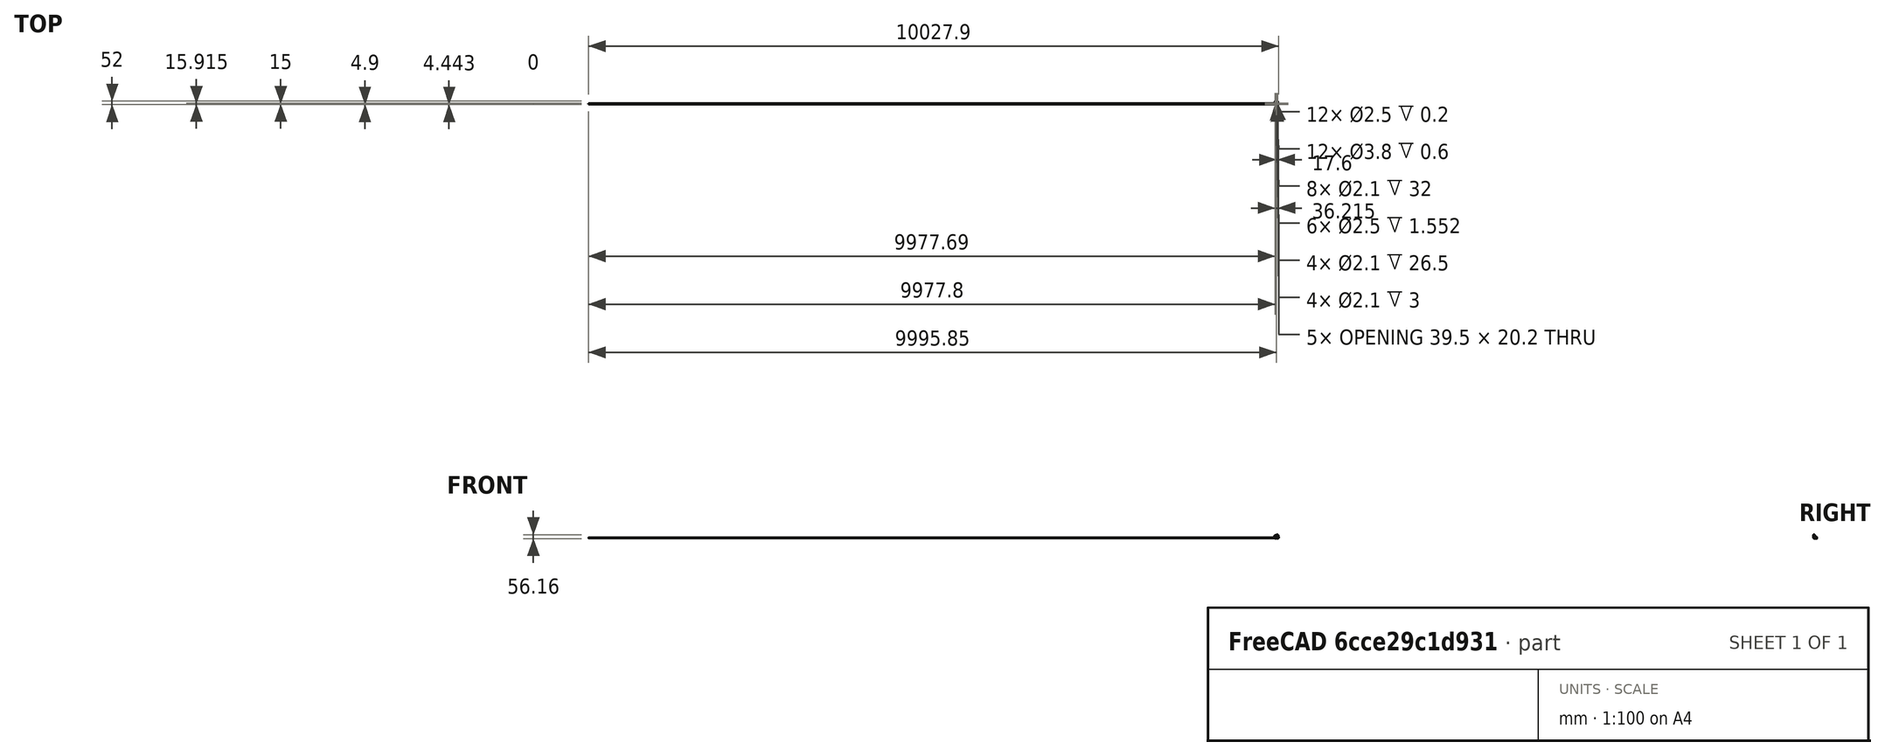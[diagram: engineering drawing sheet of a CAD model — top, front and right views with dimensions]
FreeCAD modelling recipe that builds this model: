
FCSTD DOCUMENT  (FreeCAD 0.14R3702 (Git))
Label: SM-S4303R
License: CC-BY 3.0
LicenseURL: http://creativecommons.org/licenses/by/3.0/
objects: Sketcher::SketchObject×27, Part::Feature×24, PartDesign::Pocket×12, PartDesign::Pad×9, Part::Fillet×7, Part::MultiFuse×6, App::DocumentObjectGroup×5, Part::Compound×4, Part::Loft×3, PartDesign::Mirrored×2, Part::Cut×2, PartDesign::Fillet×2, PartDesign::Chamfer×2, PartDesign::PolarPattern×1, Part::Cylinder×1
note: 123 computed .brp shape members not serialized (recipe doc carries the construction recipe); baked Part::Feature solids carry a one-line shape summary decoded from their .brp

FEATURE [Sketcher::SketchObject] Sketch  label="servo-body-sketch"
  Placement = pos=(0,0,0) rot=(1,0,0;1.5708rad)
  sketch-geometry (5):
    g0: LineSegment StartX=20.55 StartY=39.6 StartZ=0 EndX=20.55 EndY=0 EndZ=0
    g1: LineSegment StartX=20.55 StartY=0 StartZ=0 EndX=-20.55 EndY=0 EndZ=0
    g2: LineSegment StartX=-20.55 StartY=0 StartZ=0 EndX=-20.55 EndY=34.9 EndZ=0
    g3: LineSegment StartX=-20.55 StartY=34.9 StartZ=0 EndX=-12.25 EndY=39.6 EndZ=0
    g4: LineSegment StartX=-12.25 StartY=39.6 StartZ=0 EndX=20.55 EndY=39.6 EndZ=0
  constraints (15):
    c: Coincident(g0,g1)
    c: Coincident(g1,g2)
    c: Horizontal(g1)
    c: Vertical(g0)
    c: Vertical(g2)
    c: Symmetric(g1,g0,g-2)
    c: PointOnObject(g1,g-1)
    c: DistanceX(g1) = -41.1
    c: DistanceY(g0) = -39.6
    c: Coincident(g3,g2)
    c: Horizontal(g4)
    c: Coincident(g4,g0)
    c: Coincident(g3,g4)
    c: DistanceY(g2) = 34.9
    c: DistanceX(g4) = 32.8
FEATURE [PartDesign::Pad] Pad  label="servo-body-1"
  Length = 20.8
  Length2 = 100
  Midplane = true
  Placement = pos=(0,0,0) rot=(1,0,0;1.5708rad)
  Sketch = -> Sketch
  Type = 0
FEATURE [Sketcher::SketchObject] Sketch001  label="bottom-master-sketch"
  ExternalGeometry = -> [Pad]
  Placement = pos=(0,0,0) rot=(1,0,0;3.14159rad)
  Support = -> Pad [Face2]
  sketch-geometry (15):
    g0: LineSegment [constr] StartX=-20.55 StartY=10.4 StartZ=0 EndX=-18.2075 EndY=8.05754 EndZ=0
    g1: Circle [constr] CenterX=-18.2075 CenterY=8.05754 CenterZ=0 NormalX=0 NormalY=0 NormalZ=1 Radius=1.05
    g2: GeomPoint [constr] X=-18.95 Y=8.8 Z=0
    g3: LineSegment [constr] StartX=-18.2075 StartY=8.05754 StartZ=0 EndX=-18.2075 EndY=6 EndZ=0
    g4: LineSegment [constr] StartX=-18.2075 StartY=8.05754 StartZ=0 EndX=-16.15 EndY=8.05754 EndZ=0
    g5: LineSegment StartX=-20.55 StartY=6 StartZ=0 EndX=-20.55 EndY=10.4 EndZ=0
    g6: LineSegment StartX=-20.55 StartY=10.4 StartZ=0 EndX=-16.15 EndY=10.4 EndZ=0
    g7: LineSegment StartX=-16.15 StartY=10.4 StartZ=0 EndX=-16.15 EndY=8.05754 EndZ=0
    g8: ArcOfCircle CenterX=-18.2075 CenterY=8.05754 CenterZ=0 NormalX=0 NormalY=0 NormalZ=1 Radius=2.05754 StartAngle=4.71239 EndAngle=6.28319
    g9: LineSegment StartX=-20.55 StartY=6 StartZ=0 EndX=-18.2075 EndY=6 EndZ=0
    g10: ArcOfCircle CenterX=-18.2075 CenterY=-8.05754 CenterZ=0 NormalX=0 NormalY=0 NormalZ=1 Radius=2.05754 StartAngle=5.46325e-06 EndAngle=1.5708
    g11: LineSegment StartX=-18.2075 StartY=-6 StartZ=0 EndX=-20.55 EndY=-6 EndZ=0
    g12: LineSegment StartX=-20.55 StartY=-6 StartZ=0 EndX=-20.55 EndY=-10.4 EndZ=0
    g13: LineSegment StartX=-20.55 StartY=-10.4 StartZ=0 EndX=-16.15 EndY=-10.4 EndZ=0
    g14: LineSegment StartX=-16.15 StartY=-10.4 StartZ=0 EndX=-16.15 EndY=-8.05753 EndZ=0
  constraints (40):
    c: Coincident(g0,g-4)
    c: Angle(g-4,g0) = 0.785398
    c: Radius(g1) = 1.05
    c: Coincident(g1,g0)
    c: PointOnObject(g2,g0)
    c: PointOnObject(g2,g1)
    c: DistanceX(g2,g0) = -1.6
    c: Vertical(g3)
    c: Coincident(g3,g0)
    c: Coincident(g0,g4)
    c: Horizontal(g4)
    c: Equal(g3,g4)
    c: Coincident(g5,g6)
    c: Vertical(g5)
    c: Horizontal(g6)
    c: Vertical(g7)
    c: Coincident(g7,g6)
    c: Coincident(g7,g4)
    c: Coincident(g5,g0)
    c: Coincident(g8,g0)
    c: Coincident(g8,g4)
    c: Coincident(g3,g8)
    c: Coincident(g9,g5)
    c: Coincident(g9,g3)
    c: Horizontal(g9)
    c: DistanceY(g0,g5) = -4.4
    c: Horizontal(g11)
    c: Coincident(g11,g12)
    c: Vertical(g12)
    c: Coincident(g12,g13)
    c: Horizontal(g13)
    c: Coincident(g13,g14)
    c: Vertical(g14)
    c: Coincident(g12,g-4)
    c: Symmetric(g10,g0,g-1)
    c: Symmetric(g13,g6,g-1)
    c: Symmetric(g11,g3,g-1)
    c: Equal(g10,g8)
    c: Coincident(g10,g11)
    c: Coincident(g10,g14)
FEATURE [PartDesign::Pocket] Pocket  label="bottom-master"
  Length = 1.8
  Placement = pos=(0,0,0) rot=(1,0,0;1.5708rad)
  Sketch = -> Sketch001
  Type = 0
FEATURE [PartDesign::Mirrored] Mirrored  label="bottom-1"
  MirrorPlane = -> Sketch001 [V_Axis]
  Originals = -> [Pocket]
  Placement = pos=(0,0,0) rot=(1,0,0;1.5708rad)
FEATURE [Sketcher::SketchObject] Sketch002  label="bottom-2-sketch"
  ExternalGeometry = -> [Mirrored]
  Placement = pos=(0,0,1.8) rot=(1,0,0;3.14159rad)
  Support = -> Mirrored [Face23]
  sketch-geometry (10):
    g0: LineSegment [constr] StartX=-20.55 StartY=10.4 StartZ=0 EndX=-18.85 EndY=8.7 EndZ=0
    g1: Circle [constr] CenterX=-18.1075 CenterY=7.95754 CenterZ=0 NormalX=0 NormalY=0 NormalZ=1 Radius=1.05
    g2: Circle CenterX=-18.1075 CenterY=7.95754 CenterZ=0 NormalX=0 NormalY=0 NormalZ=1 Radius=1.9
    g3: Circle CenterX=-18.1075 CenterY=-7.95754 CenterZ=0 NormalX=0 NormalY=0 NormalZ=1 Radius=1.9
    g4: Circle CenterX=18.1075 CenterY=7.95754 CenterZ=0 NormalX=0 NormalY=0 NormalZ=1 Radius=1.9
    g5: Circle CenterX=18.1075 CenterY=-7.95754 CenterZ=0 NormalX=0 NormalY=0 NormalZ=1 Radius=1.9
    g6: LineSegment [constr] StartX=-18.1075 StartY=7.95754 StartZ=0 EndX=18.1075 EndY=7.95754 EndZ=0
    g7: LineSegment [constr] StartX=18.1075 StartY=7.95754 StartZ=0 EndX=18.1075 EndY=-7.95754 EndZ=0
    g8: LineSegment [constr] StartX=18.1075 StartY=-7.95754 StartZ=0 EndX=-18.1075 EndY=-7.95754 EndZ=0
    g9: LineSegment [constr] StartX=-18.1075 StartY=-7.95754 StartZ=0 EndX=-18.1075 EndY=7.95754 EndZ=0
  constraints (24):
    c: Angle(g0,g-3) = 0.785398
    c: Coincident(g0,g-3)
    c: Radius(g1) = 1.05
    c: PointOnObject(g1,g0)
    c: PointOnObject(g0,g1)
    c: DistanceX(g0,g0) = 1.7
    c: Coincident(g2,g1)
    c: Radius(g2) = 1.9
    c: Equal(g3,g2)
    c: Equal(g2,g4)
    c: Equal(g4,g5)
    c: Coincident(g6,g7)
    c: Coincident(g7,g8)
    c: Coincident(g8,g9)
    c: Coincident(g9,g6)
    c: Horizontal(g6)
    c: Horizontal(g8)
    c: Vertical(g7)
    c: Vertical(g9)
    c: Symmetric(g6,g7,g-1)
    c: Coincident(g6,g1)
    c: Coincident(g3,g8)
    c: Coincident(g6,g4)
    c: Coincident(g5,g7)
FEATURE [PartDesign::Pocket] Pocket001  label="bottom-2"
  Length = 0.6
  Placement = pos=(0,0,0) rot=(1,0,0;1.5708rad)
  Sketch = -> Sketch002
  Type = 0
FEATURE [Sketcher::SketchObject] Sketch003  label="bottom-drills-sketch"
  ExternalGeometry = -> [Pocket001]
  Placement = pos=(0,0,2.4) rot=(1,0,0;3.14159rad)
  Support = -> Pocket001 [Face31]
  sketch-geometry (8):
    g0: Circle CenterX=-18.1075 CenterY=7.95754 CenterZ=0 NormalX=0 NormalY=0 NormalZ=1 Radius=1.05
    g1: LineSegment [constr] StartX=-18.1075 StartY=7.95754 StartZ=0 EndX=18.1075 EndY=7.95754 EndZ=0
    g2: LineSegment [constr] StartX=18.1075 StartY=7.95754 StartZ=0 EndX=18.1075 EndY=-7.95754 EndZ=0
    g3: LineSegment [constr] StartX=18.1075 StartY=-7.95754 StartZ=0 EndX=-18.1075 EndY=-7.95754 EndZ=0
    g4: LineSegment [constr] StartX=-18.1075 StartY=-7.95754 StartZ=0 EndX=-18.1075 EndY=7.95754 EndZ=0
    g5: Circle CenterX=-18.1075 CenterY=-7.95754 CenterZ=0 NormalX=0 NormalY=0 NormalZ=1 Radius=1.05
    g6: Circle CenterX=18.1075 CenterY=7.95754 CenterZ=0 NormalX=0 NormalY=0 NormalZ=1 Radius=1.05
    g7: Circle CenterX=18.1075 CenterY=-7.95754 CenterZ=0 NormalX=0 NormalY=0 NormalZ=1 Radius=1.05
  constraints (18):
    c: Coincident(g0,g-3)
    c: Radius(g0) = 1.05
    c: Coincident(g1,g2)
    c: Coincident(g2,g3)
    c: Coincident(g3,g4)
    c: Coincident(g4,g1)
    c: Horizontal(g1)
    c: Horizontal(g3)
    c: Vertical(g2)
    c: Vertical(g4)
    c: Symmetric(g1,g2,g-1)
    c: Coincident(g1,g0)
    c: Equal(g6,g5)
    c: Equal(g5,g7)
    c: Equal(g7,g0)
    c: Coincident(g3,g5)
    c: Coincident(g6,g1)
    c: Coincident(g7,g2)
FEATURE [PartDesign::Pocket] Pocket002  label="bottom-drills"
  Length = 32
  Placement = pos=(0,0,0) rot=(1,0,0;1.5708rad)
  Sketch = -> Sketch003
  Type = 0
FEATURE [Sketcher::SketchObject] Sketch004  label="top-drills-1-sketch"
  ExternalGeometry = -> [Pocket002]
  Placement = pos=(0,0,39.6) rot=(0,0,1;3.14159rad)
  Support = -> Pocket002 [Face9]
  sketch-geometry (9):
    g0: LineSegment [constr] StartX=-17.65 StartY=7.5 StartZ=0 EndX=-0.05 EndY=7.5 EndZ=0
    g1: LineSegment [constr] StartX=-0.05 StartY=7.5 StartZ=0 EndX=-0.05 EndY=-7.5 EndZ=0
    g2: LineSegment [constr] StartX=-0.05 StartY=-7.5 StartZ=0 EndX=-17.65 EndY=-7.5 EndZ=0
    g3: LineSegment [constr] StartX=-17.65 StartY=-7.5 StartZ=0 EndX=-17.65 EndY=7.5 EndZ=0
    g4: Circle CenterX=-0.05 CenterY=-7.5 CenterZ=0 NormalX=0 NormalY=0 NormalZ=1 Radius=1.25
    g5: Circle CenterX=-17.65 CenterY=-7.5 CenterZ=0 NormalX=0 NormalY=0 NormalZ=1 Radius=1.25
    g6: Circle CenterX=-0.05 CenterY=7.5 CenterZ=0 NormalX=0 NormalY=0 NormalZ=1 Radius=1.25
    g7: Circle CenterX=-17.65 CenterY=7.5 CenterZ=0 NormalX=0 NormalY=0 NormalZ=1 Radius=1.25
    g8: LineSegment [constr] StartX=-20.55 StartY=-10.4 StartZ=0 EndX=-17.65 EndY=-7.5 EndZ=0
  constraints (22):
    c: Coincident(g0,g1)
    c: Coincident(g1,g2)
    c: Coincident(g2,g3)
    c: Coincident(g3,g0)
    c: Horizontal(g0)
    c: Horizontal(g2)
    c: Vertical(g1)
    c: Vertical(g3)
    c: Symmetric(g2,g0,g-1)
    c: Equal(g4,g7)
    c: Equal(g7,g6)
    c: Equal(g6,g5)
    c: Radius(g4) = 1.25
    c: Coincident(g4,g1)
    c: Coincident(g6,g0)
    c: Coincident(g5,g2)
    c: Coincident(g7,g0)
    c: DistanceY(g-1,g1) = -7.5
    c: DistanceX(g2) = -17.6
    c: Coincident(g8,g-3)
    c: Coincident(g8,g2)
    c: Angle(g-3,g8) = 0.785398
FEATURE [PartDesign::Pocket] Pocket003  label="top-drills-1"
  Length = 0.2
  Placement = pos=(0,0,0) rot=(1,0,0;1.5708rad)
  Sketch = -> Sketch004
  Type = 0
FEATURE [Sketcher::SketchObject] Sketch006  label="potentiometer-1-sketch"
  Placement = pos=(20.55,0,0) rot=(0.707107,0,0.707107;3.14159rad)
  Support = -> Pocket003 [Face1]
  sketch-geometry (2):
    g0: Circle CenterX=14.175 CenterY=0 CenterZ=0 NormalX=0 NormalY=0 NormalZ=1 Radius=1.925
    g1: GeomPoint [constr] X=16.1 Y=0 Z=0
  constraints (5):
    c: PointOnObject(g0,g-1)
    c: Radius(g0) = 1.925
    c: PointOnObject(g1,g-1)
    c: PointOnObject(g1,g0)
    c: DistanceX(g-1,g1) = 16.1
FEATURE [PartDesign::Pocket] Pocket004  label="potentiometer-hole"
  Length = 2.2
  Placement = pos=(0,0,0) rot=(1,0,0;1.5708rad)
  Sketch = -> Sketch006
  Type = 0
FEATURE [Sketcher::SketchObject] Sketch007  label="potentiometer-cross-sketch"
  ExternalGeometry = -> [Pocket004]
  Placement = pos=(18.35,0,0) rot=(0.707107,0,0.707107;3.14159rad)
  Support = -> Pocket004 [Face31]
  sketch-geometry (12):
    g0: LineSegment StartX=13.675 StartY=1.65 StartZ=0 EndX=14.675 EndY=1.65 EndZ=0
    g1: LineSegment StartX=14.675 StartY=1.65 StartZ=0 EndX=14.675 EndY=0.5 EndZ=0
    g2: LineSegment StartX=14.675 StartY=-1.65 StartZ=0 EndX=13.675 EndY=-1.65 EndZ=0
    g3: LineSegment StartX=13.675 StartY=-1.65 StartZ=0 EndX=13.675 EndY=-0.5 EndZ=0
    g4: LineSegment StartX=12.525 StartY=0.5 StartZ=0 EndX=13.675 EndY=0.5 EndZ=0
    g5: LineSegment StartX=15.825 StartY=0.5 StartZ=0 EndX=15.825 EndY=-0.5 EndZ=0
    g6: LineSegment StartX=15.825 StartY=-0.5 StartZ=0 EndX=14.675 EndY=-0.5 EndZ=0
    g7: LineSegment StartX=12.525 StartY=-0.5 StartZ=0 EndX=12.525 EndY=0.5 EndZ=0
    g8: LineSegment StartX=14.675 StartY=0.5 StartZ=0 EndX=15.825 EndY=0.5 EndZ=0
    g9: LineSegment StartX=13.675 StartY=-0.5 StartZ=0 EndX=12.525 EndY=-0.5 EndZ=0
    g10: LineSegment StartX=13.675 StartY=0.5 StartZ=0 EndX=13.675 EndY=1.65 EndZ=0
    g11: LineSegment StartX=14.675 StartY=-0.5 StartZ=0 EndX=14.675 EndY=-1.65 EndZ=0
  constraints (30):
    c: Coincident(g0,g1)
    c: Coincident(g11,g2)
    c: Coincident(g2,g3)
    c: Coincident(g10,g0)
    c: Horizontal(g0)
    c: Horizontal(g2)
    c: Vertical(g1)
    c: Vertical(g3)
    c: Coincident(g8,g5)
    c: Coincident(g5,g6)
    c: Coincident(g9,g7)
    c: Coincident(g7,g4)
    c: Horizontal(g4)
    c: Horizontal(g6)
    c: Vertical(g5)
    c: Vertical(g7)
    c: Symmetric(g4,g5,g-3)
    c: Symmetric(g0,g11,g-3)
    c: Tangent(g4,g8)
    c: Tangent(g6,g9)
    c: Coincident(g3,g9)
    c: Coincident(g10,g4)
    c: Tangent(g3,g10)
    c: Coincident(g1,g8)
    c: Coincident(g11,g6)
    c: Tangent(g1,g11)
    c: Equal(g4,g10)
    c: Equal(g7,g0)
    c: DistanceX(g5,g4) = -3.3
    c: DistanceY(g5) = -1
FEATURE [PartDesign::Pocket] Pocket005  label="potentiometer-cross"
  Length = 1
  Placement = pos=(0,0,0) rot=(1,0,0;1.5708rad)
  Sketch = -> Sketch007
  Type = 0
FEATURE [Sketcher::SketchObject] Sketch008  label="label-plate-sketch"
  ExternalGeometry = -> [Pocket005]
  Placement = pos=(-19.9538,0,35.2376) rot=(-0.254782,0,0.966998;3.14159rad)
  Support = -> Pocket005 [Face15]
  sketch-geometry (8):
    g0: LineSegment StartX=-7.65321 StartY=5.15 StartZ=0 EndX=-1.15321 EndY=5.15 EndZ=0
    g1: LineSegment StartX=-0.953214 StartY=4.95 StartZ=0 EndX=-0.953214 EndY=-4.95 EndZ=0
    g2: LineSegment StartX=-1.15321 StartY=-5.15 StartZ=0 EndX=-7.65321 EndY=-5.15 EndZ=0
    g3: LineSegment StartX=-7.85321 StartY=-4.95 StartZ=0 EndX=-7.85321 EndY=4.95 EndZ=0
    g4: ArcOfCircle CenterX=-7.65321 CenterY=4.95 CenterZ=0 NormalX=0 NormalY=0 NormalZ=1 Radius=0.2 StartAngle=1.5708 EndAngle=3.14159
    g5: ArcOfCircle CenterX=-1.15321 CenterY=4.95 CenterZ=0 NormalX=0 NormalY=0 NormalZ=1 Radius=0.2 StartAngle=0 EndAngle=1.5708
    g6: ArcOfCircle CenterX=-1.15321 CenterY=-4.95 CenterZ=0 NormalX=0 NormalY=0 NormalZ=1 Radius=0.2 StartAngle=4.71239 EndAngle=6.28319
    g7: ArcOfCircle CenterX=-7.65321 CenterY=-4.95 CenterZ=0 NormalX=0 NormalY=0 NormalZ=1 Radius=0.2 StartAngle=3.14159 EndAngle=4.71239
  constraints (20):
    c: Horizontal(g0)
    c: Horizontal(g2)
    c: Vertical(g1)
    c: Vertical(g3)
    c: Tangent(g0,g4)
    c: Tangent(g3,g4)
    c: Tangent(g0,g5)
    c: Tangent(g1,g5)
    c: Tangent(g1,g6)
    c: Tangent(g2,g6)
    c: Tangent(g2,g7)
    c: Tangent(g3,g7)
    c: Equal(g4,g5)
    c: Equal(g5,g7)
    c: Equal(g7,g6)
    c: Symmetric(g5,g6,g-1)
    c: DistanceY(g0,g2) = -10.3
    c: DistanceX(g3,g1) = 6.9
    c: Radius(g4) = 0.2
    c: DistanceX(g3,g-3) = -1
FEATURE [PartDesign::Pocket] Pocket006  label="Label-plate"
  Length = 0.1
  Placement = pos=(0,0,0) rot=(1,0,0;1.5708rad)
  Sketch = -> Sketch008
  Type = 0
FEATURE [Sketcher::SketchObject] Sketch009  label="top-left-2-drills-sketch"
  Placement = pos=(0,0,39.6) rot=(0,0,1;3.14159rad)
  Support = -> Pocket006 [Face3]
  sketch-geometry (4):
    g0: Circle CenterX=18 CenterY=7.5 CenterZ=0 NormalX=0 NormalY=0 NormalZ=1 Radius=1.25
    g1: Circle CenterX=18 CenterY=-7.5 CenterZ=0 NormalX=0 NormalY=0 NormalZ=1 Radius=1.25
    g2: LineSegment [constr] StartX=18 StartY=7.5 StartZ=0 EndX=18 EndY=0 EndZ=0
    g3: LineSegment [constr] StartX=18 StartY=7.5 StartZ=0 EndX=19.25 EndY=7.5 EndZ=0
  constraints (10):
    c: Radius(g0) = 1.25
    c: Equal(g1,g0)
    c: Symmetric(g0,g1,g-1)
    c: Coincident(g2,g0)
    c: Vertical(g2)
    c: PointOnObject(g2,g-1)
    c: DistanceY(g2) = -7.5
    c: Horizontal(g3)
    c: Coincident(g3,g0)
    c: PointOnObject(g3,g0)
FEATURE [PartDesign::Pocket] Pocket007  label="top-left-2-drills"
  Length = 4.1
  Placement = pos=(0,0,0) rot=(1,0,0;1.5708rad)
  Sketch = -> Sketch009
  Type = 0
FEATURE [Sketcher::SketchObject] Sketch010  label="top-drills-cross-1-sketch"
  sketch-geometry (13):
    g0: Circle [constr] CenterX=0 CenterY=0 CenterZ=0 NormalX=0 NormalY=0 NormalZ=1 Radius=1.25
    g1: LineSegment StartX=-0.15 StartY=0.6 StartZ=0 EndX=0.15 EndY=0.6 EndZ=0
    g2: LineSegment StartX=0.15 StartY=0.6 StartZ=0 EndX=0.15 EndY=0.15 EndZ=0
    g3: LineSegment StartX=0.15 StartY=-0.6 StartZ=0 EndX=-0.15 EndY=-0.6 EndZ=0
    g4: LineSegment StartX=-0.15 StartY=-0.6 StartZ=0 EndX=-0.15 EndY=-0.15 EndZ=0
    g5: LineSegment StartX=-0.6 StartY=0.15 StartZ=0 EndX=-0.15 EndY=0.15 EndZ=0
    g6: LineSegment StartX=0.6 StartY=0.15 StartZ=0 EndX=0.6 EndY=-0.15 EndZ=0
    g7: LineSegment StartX=0.6 StartY=-0.15 StartZ=0 EndX=0.15 EndY=-0.15 EndZ=0
    g8: LineSegment StartX=-0.6 StartY=-0.15 StartZ=0 EndX=-0.6 EndY=0.15 EndZ=0
    g9: LineSegment StartX=0.15 StartY=0.15 StartZ=0 EndX=0.6 EndY=0.15 EndZ=0
    g10: LineSegment StartX=-0.15 StartY=-0.15 StartZ=0 EndX=-0.6 EndY=-0.15 EndZ=0
    g11: LineSegment StartX=-0.15 StartY=0.15 StartZ=0 EndX=-0.15 EndY=0.6 EndZ=0
    g12: LineSegment StartX=0.15 StartY=-0.15 StartZ=0 EndX=0.15 EndY=-0.6 EndZ=0
  constraints (32):
    c: Coincident(g0,g-1)
    c: Radius(g0) = 1.25
    c: Coincident(g1,g2)
    c: Coincident(g12,g3)
    c: Coincident(g3,g4)
    c: Coincident(g11,g1)
    c: Horizontal(g1)
    c: Horizontal(g3)
    c: Vertical(g2)
    c: Vertical(g4)
    c: Symmetric(g1,g12,g-1)
    c: Coincident(g9,g6)
    c: Coincident(g6,g7)
    c: Coincident(g10,g8)
    c: Coincident(g8,g5)
    c: Horizontal(g5)
    c: Horizontal(g7)
    c: Vertical(g6)
    c: Vertical(g8)
    c: Symmetric(g5,g6,g-1)
    c: Tangent(g5,g9)
    c: Tangent(g7,g10)
    c: Coincident(g4,g10)
    c: Coincident(g11,g5)
    c: Tangent(g4,g11)
    c: Coincident(g2,g9)
    c: Coincident(g12,g7)
    c: Tangent(g2,g12)
    c: Equal(g5,g11)
    c: Equal(g8,g1)
    c: DistanceX(g5,g6) = 1.2
    c: DistanceX(g1) = 0.3
FEATURE [PartDesign::Pad] Pad001  label="top-drills-cross-1"
  Length = 10
  Length2 = 100
  Sketch = -> Sketch010
  Type = 0
FEATURE [Sketcher::SketchObject] Sketch011  label="top-drills-cross-2-sketch"
  Placement = pos=(0,0,10) rot=(0,0,1;0rad)
  Support = -> Pad001 [Face14]
  sketch-geometry (1):
    g0: Circle CenterX=0 CenterY=0 CenterZ=0 NormalX=0 NormalY=0 NormalZ=1 Radius=1.25
  constraints (2):
    c: Coincident(g0,g-1)
    c: Radius(g0) = 1.25
FEATURE [PartDesign::Pad] Pad002  label="top-drills-cross-2"
  Length = 1
  Length2 = 100
  Sketch = -> Sketch011
  Type = 0
FEATURE [Part::Feature] Pad002001  label="top-drills-cross-01"
  Placement = pos=(17.65,7.5,39.2) rot=(0,0,1;0rad)
  shape: bbox 2.5 x 2.5 x 11 mm, 16 faces (baked)
FEATURE [Part::Feature] Pad002001001  label="top-drills-cross-002"
  Placement = pos=(17.65,-7.5,39.2) rot=(0,0,1;0rad)
  shape: bbox 2.5 x 2.5 x 11 mm, 16 faces (baked)
FEATURE [Part::Feature] Pad002001002  label="top-drills-cross-003"
  Placement = pos=(0.05,7.5,39.2) rot=(0,0,1;0rad)
  shape: bbox 2.5 x 2.5 x 11 mm, 16 faces (baked)
FEATURE [Part::Feature] Pad002001003  label="top-drills-cross-004"
  Placement = pos=(0.05,-7.5,39.2) rot=(0,0,1;0rad)
  shape: bbox 2.5 x 2.5 x 11 mm, 16 faces (baked)
FEATURE [Part::Feature] Pad002001003001  label="top-drills-cross-005"
  Placement = pos=(-18,7.5,35.2) rot=(0,0,1;0rad)
  shape: bbox 2.5 x 2.5 x 11 mm, 16 faces (baked)
FEATURE [Part::Feature] Pad002001003002  label="top-drills-cross-006"
  Placement = pos=(-18,-7.5,35.2) rot=(0,0,1;0rad)
  shape: bbox 2.5 x 2.5 x 11 mm, 16 faces (baked)
FEATURE [Part::MultiFuse] Fusion  label="union-of-top-crosses"
  Shapes = -> [Pad002001,Pad002001003001,Pad002001003002,Pad002001002,Pad002001003,Pad002001001]
FEATURE [Part::Cut] Cut  label="servo-body-final-1"
  Base = -> Pocket007
  Tool = -> Fusion
FEATURE [Sketcher::SketchObject] Sketch012  label="shaft-anchor-sketch"
  ExternalGeometry = -> [Cut]
  Placement = pos=(0,0,39.6) rot=(0,0,1;0rad)
  Support = -> Cut [Face3]
  sketch-geometry (2):
    g0: Circle CenterX=10.55 CenterY=0 CenterZ=0 NormalX=0 NormalY=0 NormalZ=1 Radius=3
    g1: LineSegment [constr] StartX=13.55 StartY=0 StartZ=0 EndX=20.55 EndY=0 EndZ=0
  constraints (7):
    c: PointOnObject(g0,g-1)
    c: Radius(g0) = 3
    c: Horizontal(g1)
    c: PointOnObject(g1,g-3)
    c: PointOnObject(g1,g-1)
    c: PointOnObject(g1,g0)
    c: DistanceX(g1) = 7
FEATURE [PartDesign::Pad] Pad002001003003  label="servo-body-final-2"
  Length = 0.1
  Length2 = 100
  Sketch = -> Sketch012
  Type = 0
FEATURE [Sketcher::SketchObject] Sketch013  label="side-gap-sketch"
  sketch-geometry (25):
    g0: LineSegment [constr] StartX=-18.05 StartY=10.4 StartZ=0 EndX=18.05 EndY=10.4 EndZ=0
    g1: LineSegment [constr] StartX=20.05 StartY=8.4 StartZ=0 EndX=20.05 EndY=-8.4 EndZ=0
    g2: LineSegment [constr] StartX=18.05 StartY=-10.4 StartZ=0 EndX=-18.05 EndY=-10.4 EndZ=0
    g3: LineSegment [constr] StartX=-20.05 StartY=-8.4 StartZ=0 EndX=-20.05 EndY=8.4 EndZ=0
    g4: LineSegment [constr] StartX=-22.05 StartY=12.4 StartZ=0 EndX=-18.05 EndY=8.4 EndZ=0
    g5: LineSegment StartX=-18.05 StartY=10.1 StartZ=0 EndX=18.05 EndY=10.1 EndZ=0
    g6: LineSegment StartX=19.75 StartY=8.4 StartZ=0 EndX=19.75 EndY=-8.4 EndZ=0
    g7: LineSegment StartX=18.05 StartY=-10.1 StartZ=0 EndX=-18.05 EndY=-10.1 EndZ=0
    g8: LineSegment StartX=-19.75 StartY=-8.4 StartZ=0 EndX=-19.75 EndY=8.4 EndZ=0
    g9: LineSegment StartX=-22.05 StartY=12.4 StartZ=0 EndX=22.05 EndY=12.4 EndZ=0
    g10: LineSegment StartX=22.05 StartY=12.4 StartZ=0 EndX=22.05 EndY=-12.4 EndZ=0
    g11: LineSegment StartX=22.05 StartY=-12.4 StartZ=0 EndX=-22.05 EndY=-12.4 EndZ=0
    g12: LineSegment StartX=-22.05 StartY=-12.4 StartZ=0 EndX=-22.05 EndY=12.4 EndZ=0
    g13: ArcOfCircle [constr] CenterX=18.05 CenterY=-8.4 CenterZ=0 NormalX=0 NormalY=0 NormalZ=1 Radius=2 StartAngle=4.71239 EndAngle=6.28319
    g14: ArcOfCircle [constr] CenterX=18.05 CenterY=8.4 CenterZ=0 NormalX=0 NormalY=0 NormalZ=1 Radius=2 StartAngle=0 EndAngle=1.5708
    g15: ArcOfCircle [constr] CenterX=-18.05 CenterY=8.4 CenterZ=0 NormalX=0 NormalY=0 NormalZ=1 Radius=2 StartAngle=1.5708 EndAngle=3.14159
    g16: ArcOfCircle [constr] CenterX=-18.05 CenterY=-8.4 CenterZ=0 NormalX=0 NormalY=0 NormalZ=1 Radius=2 StartAngle=3.14159 EndAngle=4.71239
    g17: LineSegment [constr] StartX=-18.05 StartY=8.4 StartZ=0 EndX=18.05 EndY=8.4 EndZ=0
    g18: LineSegment [constr] StartX=18.05 StartY=8.4 StartZ=0 EndX=18.05 EndY=-8.4 EndZ=0
    g19: LineSegment [constr] StartX=18.05 StartY=-8.4 StartZ=0 EndX=-18.05 EndY=-8.4 EndZ=0
    g20: LineSegment [constr] StartX=-18.05 StartY=-8.4 StartZ=0 EndX=-18.05 EndY=8.4 EndZ=0
    g21: ArcOfCircle CenterX=-18.05 CenterY=8.4 CenterZ=0 NormalX=0 NormalY=0 NormalZ=1 Radius=1.7 StartAngle=1.5708 EndAngle=3.14159
    g22: ArcOfCircle CenterX=-18.05 CenterY=-8.4 CenterZ=0 NormalX=0 NormalY=0 NormalZ=1 Radius=1.7 StartAngle=3.14159 EndAngle=4.71239
    g23: ArcOfCircle CenterX=18.05 CenterY=-8.4 CenterZ=0 NormalX=0 NormalY=0 NormalZ=1 Radius=1.7 StartAngle=4.71239 EndAngle=6.28319
    g24: ArcOfCircle CenterX=18.05 CenterY=8.4 CenterZ=0 NormalX=0 NormalY=0 NormalZ=1 Radius=1.7 StartAngle=0 EndAngle=1.5708
  constraints (62):
    c: Horizontal(g0)
    c: Horizontal(g2)
    c: Vertical(g1)
    c: Vertical(g3)
    c: Angle(g-1,g4) = 2.35619
    c: Horizontal(g5)
    c: Horizontal(g7)
    c: Vertical(g6)
    c: Vertical(g8)
    c: Coincident(g9,g10)
    c: Coincident(g10,g11)
    c: Coincident(g11,g12)
    c: Coincident(g12,g9)
    c: Horizontal(g9)
    c: Horizontal(g11)
    c: Vertical(g10)
    c: Vertical(g12)
    c: PointOnObject(g9,g4)
    c: Symmetric(g9,g10,g-1)
    c: Coincident(g4,g9)
    c: Tangent(g1,g13)
    c: Tangent(g2,g13)
    c: Radius(g13) = 2
    c: Tangent(g0,g14)
    c: Tangent(g1,g14)
    c: Tangent(g0,g15)
    c: Tangent(g3,g15)
    c: Tangent(g2,g16)
    c: Tangent(g3,g16)
    c: Coincident(g17,g18)
    c: Coincident(g18,g19)
    c: Coincident(g19,g20)
    c: Coincident(g20,g17)
    c: Horizontal(g17)
    c: Horizontal(g19)
    c: Vertical(g18)
    c: Vertical(g20)
    c: Coincident(g17,g15)
    c: Symmetric(g15,g18,g-1)
    c: PointOnObject(g15,g4)
    c: Equal(g15,g16)
    c: Equal(g16,g14)
    c: Equal(g14,g13)
    c: DistanceX(g3,g1) = 40.1
    c: DistanceY(g0,g2) = -20.8
    c: Tangent(g8,g21)
    c: Tangent(g5,g21)
    c: PointOnObject(g21,g4)
    c: Coincident(g21,g15)
    c: Coincident(g4,g15)
    c: DistanceX(g8,g3) = -0.3
    c: DistanceX(g3,g4) = -2
    c: Tangent(g8,g22)
    c: Tangent(g7,g22)
    c: Coincident(g22,g16)
    c: Tangent(g7,g23)
    c: Tangent(g6,g23)
    c: Coincident(g23,g18)
    c: Tangent(g5,g24)
    c: Tangent(g6,g24)
    c: Coincident(g24,g17)
    c: Coincident(g14,g17)
FEATURE [PartDesign::Pad] Pad002001003004  label="side-gap-master"
  Length = 0.4
  Length2 = 100
  Sketch = -> Sketch013
  Type = 0
FEATURE [Sketcher::SketchObject] Sketch014  label="servo-top-1-sketch"
  sketch-geometry (10):
    g0: LineSegment [constr] StartX=-9.03485 StartY=1.65 StartZ=0 EndX=-9.03485 EndY=-1.65 EndZ=0
    g1: ArcOfCircle CenterX=-9.03485 CenterY=0 CenterZ=0 NormalX=0 NormalY=0 NormalZ=1 Radius=1.65 StartAngle=1.5708 EndAngle=4.71239
    g2: LineSegment StartX=-9.03485 StartY=1.65 StartZ=0 EndX=-2.38485 EndY=1.65 EndZ=0
    g3: LineSegment StartX=-9.03485 StartY=-1.65 StartZ=0 EndX=-2.38485 EndY=-1.65 EndZ=0
    g4: LineSegment StartX=11.1848 StartY=1.65 StartZ=0 EndX=11.1848 EndY=-1.65 EndZ=0
    g5: ArcOfCircle CenterX=0 CenterY=0 CenterZ=0 NormalX=0 NormalY=0 NormalZ=1 Radius=2.9 StartAngle=3.74684 EndAngle=5.67794
    g6: LineSegment StartX=2.38485 StartY=1.65 StartZ=0 EndX=11.1848 EndY=1.65 EndZ=0
    g7: ArcOfCircle CenterX=0 CenterY=0 CenterZ=0 NormalX=0 NormalY=0 NormalZ=1 Radius=2.9 StartAngle=0.605247 EndAngle=2.53635
    g8: LineSegment StartX=2.38485 StartY=-1.65 StartZ=0 EndX=11.1848 EndY=-1.65 EndZ=0
    g9: Circle [constr] CenterX=11.1848 CenterY=0 CenterZ=0 NormalX=0 NormalY=0 NormalZ=1 Radius=6.7
  constraints (29):
    c: Vertical(g0)
    c: Symmetric(g0,g0,g-1)
    c: Coincident(g1,g0)
    c: Coincident(g0,g1)
    c: PointOnObject(g1,g0)
    c: Horizontal(g2)
    c: Coincident(g2,g0)
    c: Horizontal(g3)
    c: Coincident(g3,g0)
    c: Coincident(g6,g4)
    c: Vertical(g4)
    c: Coincident(g4,g8)
    c: Tangent(g2,g6)
    c: PointOnObject(g7,g2)
    c: Equal(g5,g7)
    c: Coincident(g7,g6)
    c: Coincident(g5,g7)
    c: Coincident(g3,g5)
    c: Coincident(g8,g5)
    c: Tangent(g3,g8)
    c: Coincident(g7,g2)
    c: Coincident(g5,g-1)
    c: DistanceY(g0) = -3.3
    c: DistanceX(g0,g2) = 6.65
    c: Radius(g7) = 2.9
    c: Radius(g9) = 6.7
    c: PointOnObject(g9,g-1)
    c: PointOnObject(g9,g4)
    c: DistanceX(g6,g9) = 8.8
FEATURE [Sketcher::SketchObject] Sketch015  label="servo-top-1-sketch2"
  Placement = pos=(0,0,1.16) rot=(0,0,1;0rad)
  sketch-geometry (10):
    g0: LineSegment [constr] StartX=-8.99374 StartY=1.3 StartZ=0 EndX=-8.99374 EndY=-1.3 EndZ=0
    g1: ArcOfCircle CenterX=-8.99374 CenterY=0 CenterZ=0 NormalX=0 NormalY=0 NormalZ=1 Radius=1.3 StartAngle=1.5708 EndAngle=4.71239
    g2: LineSegment StartX=-8.99374 StartY=1.3 StartZ=0 EndX=-2.19374 EndY=1.3 EndZ=0
    g3: LineSegment StartX=-8.99374 StartY=-1.3 StartZ=0 EndX=-2.19374 EndY=-1.3 EndZ=0
    g4: LineSegment StartX=11.1937 StartY=1.3 StartZ=0 EndX=11.1937 EndY=-1.3 EndZ=0
    g5: ArcOfCircle CenterX=0 CenterY=0 CenterZ=0 NormalX=0 NormalY=0 NormalZ=1 Radius=2.55 StartAngle=3.67655 EndAngle=5.74823
    g6: LineSegment StartX=2.19374 StartY=1.3 StartZ=0 EndX=11.1937 EndY=1.3 EndZ=0
    g7: ArcOfCircle CenterX=0 CenterY=0 CenterZ=0 NormalX=0 NormalY=0 NormalZ=1 Radius=2.55 StartAngle=0.534957 EndAngle=2.60664
    g8: LineSegment StartX=2.19374 StartY=-1.3 StartZ=0 EndX=11.1937 EndY=-1.3 EndZ=0
    g9: Circle [constr] CenterX=11.1937 CenterY=0 CenterZ=0 NormalX=0 NormalY=0 NormalZ=1 Radius=6.7
  constraints (29):
    c: Vertical(g0)
    c: Symmetric(g0,g0,g-1)
    c: Coincident(g1,g0)
    c: Coincident(g0,g1)
    c: PointOnObject(g1,g0)
    c: Horizontal(g2)
    c: Coincident(g2,g0)
    c: Horizontal(g3)
    c: Coincident(g3,g0)
    c: Coincident(g6,g4)
    c: Vertical(g4)
    c: Coincident(g4,g8)
    c: Tangent(g2,g6)
    c: PointOnObject(g7,g2)
    c: Equal(g5,g7)
    c: Coincident(g7,g6)
    c: Coincident(g5,g7)
    c: Coincident(g3,g5)
    c: Coincident(g8,g5)
    c: Tangent(g3,g8)
    c: Coincident(g7,g2)
    c: Coincident(g5,g-1)
    c: DistanceY(g0) = -2.6
    c: DistanceX(g0,g2) = 6.8
    c: Radius(g7) = 2.55
    c: Radius(g9) = 6.7
    c: PointOnObject(g9,g-1)
    c: PointOnObject(g9,g4)
    c: DistanceX(g6,g9) = 9
FEATURE [Part::Loft] Loft  label="servo-top-1"
  Closed = false
  Ruled = false
  Sections = -> [Sketch014,Sketch015]
  Solid = true
FEATURE [Sketcher::SketchObject] Sketch016  label="shaft-base-1-sketch"
  sketch-geometry (1):
    g0: Circle CenterX=0 CenterY=0 CenterZ=0 NormalX=0 NormalY=0 NormalZ=1 Radius=6.7
  constraints (2):
    c: Radius(g0) = 6.7
    c: Coincident(g-1,g0)
FEATURE [Sketcher::SketchObject] Sketch017  label="shaft-base-1-sketch2"
  Placement = pos=(0,0,2.2) rot=(0,0,1;0rad)
  sketch-geometry (1):
    g0: Circle CenterX=0 CenterY=0 CenterZ=0 NormalX=0 NormalY=0 NormalZ=1 Radius=5.85
  constraints (2):
    c: Radius(g0) = 5.85
    c: Coincident(g-1,g0)
FEATURE [Part::Loft] Loft001  label="Shaft-base-1"
  Closed = false
  Placement = pos=(11.1848,0,0) rot=(0,0,1;0rad)
  Ruled = false
  Sections = -> [Sketch016,Sketch017]
  Solid = true
FEATURE [Part::MultiFuse] Fusion002  label="top-part-1"
  Shapes = -> [Loft,Loft001]
FEATURE [PartDesign::Fillet] Fillet
  Base = -> Fusion002 [Edge25]
  Radius = 0.5
FEATURE [Part::Fillet] Fillet001  label="top-part-2"
  Base = -> Fillet
  Edges = 8 edges r=0.1: [Edge6,Edge17,Edge19,Edge20,Edge21,Edge22,Edge23,Edge24]
FEATURE [App::DocumentObjectGroup] Group001  label="top-part-src"
  Group = -> [Fusion002,Fillet001]
FEATURE [Part::Feature] Fillet002  label="top-part"
  Placement = pos=(-0.634848,0,39.7) rot=(0,0,1;0rad)
  shape: bbox 28.82 x 13.4 x 14.16 mm, 24 faces (baked)
FEATURE [Sketcher::SketchObject] Sketch019  label="ears-body-1-sketch"
  sketch-geometry (4):
    g0: LineSegment StartX=-28 StartY=9.6 StartZ=0 EndX=28 EndY=9.6 EndZ=0
    g1: LineSegment StartX=28 StartY=9.6 StartZ=0 EndX=28 EndY=-9.6 EndZ=0
    g2: LineSegment StartX=28 StartY=-9.6 StartZ=0 EndX=-28 EndY=-9.6 EndZ=0
    g3: LineSegment StartX=-28 StartY=-9.6 StartZ=0 EndX=-28 EndY=9.6 EndZ=0
  constraints (11):
    c: Coincident(g0,g1)
    c: Coincident(g1,g2)
    c: Coincident(g2,g3)
    c: Coincident(g3,g0)
    c: Horizontal(g0)
    c: Horizontal(g2)
    c: Vertical(g1)
    c: Vertical(g3)
    c: Symmetric(g0,g1,g-1)
    c: DistanceX(g0) = 56
    c: DistanceY(g3) = 19.2
FEATURE [PartDesign::Pad] Pad002001003004001002  label="ears-body-1"
  Length = 2.5
  Length2 = 100
  Sketch = -> Sketch019
  Type = 0
FEATURE [Sketcher::SketchObject] Sketch020  label="right-ears-sketch"
  Placement = pos=(0,0,2.5) rot=(0,0,1;0rad)
  Support = -> Pad002001003004001002 [Face6]
  sketch-geometry (9):
    g0: ArcOfCircle CenterX=25.15 CenterY=5.1 CenterZ=0 NormalX=0 NormalY=0 NormalZ=1 Radius=2.25 StartAngle=0.605154 EndAngle=5.67803
    g1: LineSegment [constr] StartX=22.9 StartY=5.1 StartZ=0 EndX=25.15 EndY=5.1 EndZ=0
    g2: LineSegment StartX=27.0004 StartY=6.38 StartZ=0 EndX=29.0004 EndY=6.38 EndZ=0
    g3: LineSegment StartX=29.0004 StartY=6.38 StartZ=0 EndX=29.0004 EndY=3.82 EndZ=0
    g4: LineSegment StartX=29.0004 StartY=3.82 StartZ=0 EndX=27.0004 EndY=3.82 EndZ=0
    g5: ArcOfCircle CenterX=25.15 CenterY=-5.1 CenterZ=0 NormalX=0 NormalY=0 NormalZ=1 Radius=2.25 StartAngle=0.605154 EndAngle=5.67803
    g6: LineSegment StartX=27.0004 StartY=-3.82 StartZ=0 EndX=29.0004 EndY=-3.82 EndZ=0
    g7: LineSegment StartX=29.0004 StartY=-3.82 StartZ=0 EndX=29.0004 EndY=-6.38 EndZ=0
    g8: LineSegment StartX=29.0004 StartY=-6.38 StartZ=0 EndX=27.0004 EndY=-6.38 EndZ=0
  constraints (28):
    c: Radius(g0) = 2.25
    c: DistanceX(g0) = 25.15
    c: DistanceY(g0) = 5.1
    c: Horizontal(g1)
    c: PointOnObject(g1,g0)
    c: Coincident(g1,g0)
    c: Coincident(g2,g3)
    c: Coincident(g3,g4)
    c: Horizontal(g2)
    c: Horizontal(g4)
    c: Vertical(g3)
    c: Coincident(g0,g2)
    c: Coincident(g0,g4)
    c: Symmetric(g0,g0,g1)
    c: DistanceY(g3) = -2.56
    c: DistanceX(g2) = 2
    c: Symmetric(g5,g0,g-1)
    c: Equal(g0,g5)
    c: Coincident(g6,g7)
    c: Coincident(g7,g8)
    c: Horizontal(g6)
    c: Horizontal(g8)
    c: Vertical(g7)
    c: Coincident(g6,g5)
    c: Coincident(g8,g5)
    c: Symmetric(g5,g0,g-1)
    c: Symmetric(g0,g5,g-1)
    c: Symmetric(g6,g3,g-1)
FEATURE [PartDesign::Pocket] Pocket008  label="right-ear"
  Length = 5
  Sketch = -> Sketch020
  Type = 1
FEATURE [PartDesign::Mirrored] Mirrored001  label="ears-block-1"
  MirrorPlane = -> Sketch020 [V_Axis]
  Originals = -> [Pocket008]
FEATURE [Sketcher::SketchObject] Sketch021  label="ears-block-2-sketch"
  Placement = pos=(0,0,2.5) rot=(0,0,1;0rad)
  Support = -> Mirrored001 [Face5]
  sketch-geometry (6):
    g0: ArcOfCircle CenterX=-23.8 CenterY=0 CenterZ=0 NormalX=0 NormalY=0 NormalZ=1 Radius=1 StartAngle=1.57079 EndAngle=4.7124
    g1: ArcOfCircle CenterX=23.8 CenterY=0 CenterZ=0 NormalX=0 NormalY=0 NormalZ=1 Radius=1 StartAngle=4.71238 EndAngle=7.85399
    g2: LineSegment StartX=-23.8 StartY=-1 StartZ=0 EndX=23.8 EndY=-1 EndZ=0
    g3: LineSegment StartX=-23.8 StartY=1 StartZ=0 EndX=23.8 EndY=1 EndZ=0
    g4: GeomPoint [constr] X=-24.8 Y=0 Z=0
    g5: GeomPoint [constr] X=24.8 Y=0 Z=0
  constraints (18):
    c: Tangent(g0,g2)
    c: Tangent(g0,g3)
    c: Tangent(g1,g2)
    c: Tangent(g1,g3)
    c: Coincident(g0,g3)
    c: Coincident(g0,g2)
    c: Coincident(g2,g1)
    c: Coincident(g3,g1)
    c: Horizontal(g2)
    c: Equal(g0,g1)
    c: Symmetric(g0,g1,g-2)
    c: PointOnObject(g0,g-1)
    c: DistanceY(g0,g0) = 2
    c: PointOnObject(g4,g-1)
    c: PointOnObject(g4,g0)
    c: PointOnObject(g5,g-1)
    c: PointOnObject(g5,g1)
    c: DistanceX(g4,g5) = 49.6
FEATURE [PartDesign::Pad] Pad002001003004001003  label="ears-block-2"
  Length = 0.86
  Length2 = 100
  Sketch = -> Sketch021
  Type = 0
FEATURE [Sketcher::SketchObject] Sketch022  label="wire-holder-base-sketch"
  Placement = pos=(0,0,0) rot=(0.57735,0.57735,0.57735;2.0944rad)
  sketch-geometry (4):
    g0: LineSegment StartX=-3.4 StartY=2.15 StartZ=0 EndX=3.4 EndY=2.15 EndZ=0
    g1: LineSegment StartX=3.4 StartY=2.15 StartZ=0 EndX=3.4 EndY=-2.15 EndZ=0
    g2: LineSegment StartX=3.4 StartY=-2.15 StartZ=0 EndX=-3.4 EndY=-2.15 EndZ=0
    g3: LineSegment StartX=-3.4 StartY=-2.15 StartZ=0 EndX=-3.4 EndY=2.15 EndZ=0
  constraints (11):
    c: Coincident(g0,g1)
    c: Coincident(g1,g2)
    c: Coincident(g2,g3)
    c: Coincident(g3,g0)
    c: Horizontal(g0)
    c: Horizontal(g2)
    c: Vertical(g1)
    c: Vertical(g3)
    c: Symmetric(g0,g1,g-1)
    c: DistanceY(g1) = -4.3
    c: DistanceX(g0) = 6.8
FEATURE [PartDesign::Pad] Pad002001003004001005  label="wire-holder-base"
  Length = 1.5
  Length2 = 100
  Placement = pos=(0,0,0) rot=(0.57735,0.57735,0.57735;2.0944rad)
  Sketch = -> Sketch022
  Type = 0
FEATURE [Sketcher::SketchObject] Sketch023  label="wire-holder-body-1-sketch"
  Placement = pos=(0,0,0) rot=(0.57735,0.57735,0.57735;2.0944rad)
  sketch-geometry (4):
    g0: LineSegment StartX=-2.975 StartY=1.85 StartZ=0 EndX=2.975 EndY=1.85 EndZ=0
    g1: LineSegment StartX=2.975 StartY=1.85 StartZ=0 EndX=2.975 EndY=-1.85 EndZ=0
    g2: LineSegment StartX=2.975 StartY=-1.85 StartZ=0 EndX=-2.975 EndY=-1.85 EndZ=0
    g3: LineSegment StartX=-2.975 StartY=-1.85 StartZ=0 EndX=-2.975 EndY=1.85 EndZ=0
  constraints (11):
    c: Coincident(g0,g1)
    c: Coincident(g1,g2)
    c: Coincident(g2,g3)
    c: Coincident(g3,g0)
    c: Horizontal(g0)
    c: Horizontal(g2)
    c: Vertical(g1)
    c: Vertical(g3)
    c: Symmetric(g0,g1,g-1)
    c: DistanceX(g0) = 5.95
    c: DistanceY(g3) = 3.7
FEATURE [Sketcher::SketchObject] Sketch024  label="wire-holder-body-1-sketch2"
  Placement = pos=(4.2,0,0) rot=(0.57735,0.57735,0.57735;2.0944rad)
  sketch-geometry (4):
    g0: LineSegment StartX=-2.7 StartY=1.55 StartZ=0 EndX=2.7 EndY=1.55 EndZ=0
    g1: LineSegment StartX=2.7 StartY=1.55 StartZ=0 EndX=2.7 EndY=-1.55 EndZ=0
    g2: LineSegment StartX=2.7 StartY=-1.55 StartZ=0 EndX=-2.7 EndY=-1.55 EndZ=0
    g3: LineSegment StartX=-2.7 StartY=-1.55 StartZ=0 EndX=-2.7 EndY=1.55 EndZ=0
  constraints (11):
    c: Coincident(g0,g1)
    c: Coincident(g1,g2)
    c: Coincident(g2,g3)
    c: Coincident(g3,g0)
    c: Horizontal(g0)
    c: Horizontal(g2)
    c: Vertical(g1)
    c: Vertical(g3)
    c: Symmetric(g0,g1,g-1)
    c: DistanceX(g0) = 5.4
    c: DistanceY(g1) = -3.1
FEATURE [Part::Loft] Loft002  label="wire-holder-body-1"
  Closed = false
  Ruled = false
  Sections = -> [Sketch023,Sketch024]
  Solid = true
FEATURE [Sketcher::SketchObject] Sketch025  label="wire-holes-sketch"
  Placement = pos=(4.2,0,0) rot=(0.57735,0.57735,0.57735;2.0944rad)
  Support = -> Loft002 [Face6]
  sketch-geometry (8):
    g0: ArcOfCircle CenterX=-1.2 CenterY=0 CenterZ=0 NormalX=0 NormalY=0 NormalZ=1 Radius=0.7 StartAngle=0.666946 EndAngle=5.61624
    g1: LineSegment StartX=-0.65 StartY=0.433013 StartZ=0 EndX=-0.55 EndY=0.433013 EndZ=0
    g2: ArcOfCircle CenterX=0 CenterY=0 CenterZ=0 NormalX=0 NormalY=0 NormalZ=1 Radius=0.7 StartAngle=0.666946 EndAngle=2.47465
    g3: LineSegment StartX=0.55 StartY=0.433013 StartZ=0 EndX=0.65 EndY=0.433013 EndZ=0
    g4: LineSegment StartX=-0.65 StartY=-0.433013 StartZ=0 EndX=-0.55 EndY=-0.433013 EndZ=0
    g5: ArcOfCircle CenterX=0 CenterY=0 CenterZ=0 NormalX=0 NormalY=0 NormalZ=1 Radius=0.7 StartAngle=3.80854 EndAngle=5.61624
    g6: ArcOfCircle CenterX=1.2 CenterY=0 CenterZ=0 NormalX=0 NormalY=0 NormalZ=1 Radius=0.7 StartAngle=3.80854 EndAngle=8.75783
    g7: LineSegment StartX=0.55 StartY=-0.433013 StartZ=0 EndX=0.65 EndY=-0.433013 EndZ=0
  constraints (26):
    c: PointOnObject(g0,g-1)
    c: Horizontal(g1)
    c: Coincident(g1,g0)
    c: Coincident(g3,g6)
    c: Coincident(g1,g2)
    c: Coincident(g3,g2)
    c: Tangent(g1,g3)
    c: Horizontal(g4)
    c: Symmetric(g0,g4,g-1)
    c: PointOnObject(g0,g4)
    c: PointOnObject(g6,g4)
    c: Coincident(g4,g5)
    c: Coincident(g7,g5)
    c: Tangent(g4,g7)
    c: PointOnObject(g7,g6)
    c: Equal(g1,g4)
    c: Equal(g4,g3)
    c: Equal(g3,g7)
    c: Equal(g5,g0)
    c: Equal(g0,g2)
    c: Equal(g2,g6)
    c: Radius(g6) = 0.7
    c: DistanceX(g0,g6) = 2.4
    c: Coincident(g5,g-1)
    c: Coincident(g2,g-1)
    c: DistanceX(g1) = 0.1
FEATURE [PartDesign::Pocket] Pocket009  label="wire-holder-body-2"
  Length = 5
  Sketch = -> Sketch025
  Type = 1
FEATURE [Part::Feature] Pocket010  label="wire-holder-body-2-copy"
  Placement = pos=(1.5,0,0) rot=(0,0,1;0rad)
  shape: bbox 4.2 x 5.95 x 3.7 mm, 14 faces (baked)
FEATURE [Part::MultiFuse] Fusion003  label="wire-holder-body-3"
  Shapes = -> [Pad002001003004001005,Pocket010]
FEATURE [Part::Fillet] Fillet003  label="wire-holder-body-4"
  Base = -> Fusion003
  Edges = 8 edges r=0.5: [Edge1,Edge2,Edge5,Edge8,Edge17,Edge18,Edge20,Edge22]
FEATURE [App::DocumentObjectGroup] Group003  label="wire-holder-src"
  Group = -> [Pad002001003004001005,Loft002,Pocket009,Pocket010,Fusion003,Fillet003]
FEATURE [Part::Feature] Fillet003001  label="wire-holder"
  Placement = pos=(20.55,0,6.35) rot=(0,0,1;0rad)
  shape: bbox 5.992 x 6.8 x 4.3 mm, 28 faces (baked)
FEATURE [Part::Fillet] Fillet003002
  Base = -> Pad002001003004001003
  Edges = 4 edges r=0.8: [Edge33,Edge34,Edge69,Edge71]
FEATURE [Part::Fillet] Fillet003003
  Base = -> Fillet003002
  Edges = 16 edges r=0.6: [Edge37,Edge39,Edge41,Edge43,Edge44,Edge46,Edge49,Edge51,Edge53,Edge55,Edge57,Edge59,Edge60,Edge62,Edge65,Edge67]
FEATURE [Part::Fillet] Fillet003004  label="ears-block-3"
  Base = -> Fillet003003
  Edges = 1 edges r=0.2: [Edge36]
FEATURE [Part::Fillet] Fillet003005  label="ears-block-4"
  Base = -> Fillet003004
  Edges = 1 edges r=0.2: [Edge132]
FEATURE [App::DocumentObjectGroup] Group002  label="ears-src"
  Group = -> [Pad002001003004001002,Pocket008,Mirrored001,Pad002001003004001003,Fillet003004,Fillet003005]
FEATURE [Part::Feature] Fillet003005001  label="ears"
  Placement = pos=(0,0,28.9) rot=(0,0,1;0rad)
  shape: bbox 56.13 x 19.33 x 3.36 mm, 91 faces (baked)
FEATURE [Sketcher::SketchObject] Sketch026  label="shaft-body-sketch"
  sketch-geometry (1):
    g0: Circle CenterX=0 CenterY=0 CenterZ=0 NormalX=0 NormalY=0 NormalZ=1 Radius=3
  constraints (2):
    c: Coincident(g0,g-1)
    c: Radius(g0) = 3
FEATURE [PartDesign::Pad] Pad002001003004001006  label="shaft-body"
  Length = 4.4
  Length2 = 100
  Sketch = -> Sketch026
  Type = 0
FEATURE [Sketcher::SketchObject] Sketch027  label="shaft-body-2-sketch"
  Placement = pos=(0,0,4.4) rot=(0,0,1;0rad)
  Support = -> Pad002001003004001006 [Face3]
  sketch-geometry (1):
    g0: Circle CenterX=0 CenterY=0 CenterZ=0 NormalX=0 NormalY=0 NormalZ=1 Radius=1.1
  constraints (2):
    c: Coincident(g0,g-1)
    c: Radius(g0) = 1.1
FEATURE [PartDesign::Pocket] Pocket011  label="shaft-body-2"
  Length = 5
  Sketch = -> Sketch027
  Type = 1
FEATURE [PartDesign::Chamfer] Chamfer  label="shaft-body-3"
  Base = -> Pocket011 [Edge3]
  Size = 0.3
FEATURE [Sketcher::SketchObject] Sketch028  label="shaft-tooth-sketch"
  Placement = pos=(0,0,4.4) rot=(0,0,1;0rad)
  Support = -> Chamfer [Face4]
  sketch-geometry (3):
    g0: LineSegment StartX=-0.2 StartY=3 StartZ=0 EndX=0 EndY=2.8 EndZ=0
    g1: LineSegment StartX=0.2 StartY=3 StartZ=0 EndX=0 EndY=2.8 EndZ=0
    g2: LineSegment StartX=-0.2 StartY=3 StartZ=0 EndX=0.2 EndY=3 EndZ=0
  constraints (8):
    c: Horizontal(g2)
    c: Coincident(g2,g0)
    c: Coincident(g2,g1)
    c: Symmetric(g0,g1,g-2)
    c: DistanceX(g2) = 0.4
    c: Coincident(g0,g1)
    c: PointOnObject(g0,g-2)
    c: DistanceY(g0,g1) = 0.2
FEATURE [PartDesign::Pocket] Pocket012  label="shaft-tooth"
  Length = 3.4
  Sketch = -> Sketch028
  Type = 0
FEATURE [PartDesign::PolarPattern] PolarPattern  label="shaft-teeth"
  Angle = 360
  Axis = -> Sketch028 [N_Axis]
  Occurrences = 28
  Originals = -> [Pocket012]
FEATURE [PartDesign::Chamfer] Chamfer001  label="shaft-final"
  Base = -> PolarPattern [Edge286]
  Size = 0.3
FEATURE [App::DocumentObjectGroup] Group004  label="shaft-src"
  Group = -> [Pad002001003004001006,Pocket011,Chamfer,Pocket012,PolarPattern,Chamfer001]
FEATURE [Part::Feature] Chamfer001001  label="shaft"
  Placement = pos=(10.55,0,41.9) rot=(0,0,1;0rad)
  shape: bbox 6 x 6 x 4.4 mm, 90 faces (baked)
FEATURE [Part::Feature] Pad002001003004001007  label="bottom-side-gap"
  Placement = pos=(0,0,7.5) rot=(0,0,1;0rad)
  shape: bbox 44.1 x 24.8 x 0.4 mm, 14 faces (baked)
FEATURE [Part::Feature] Pad002001003004001007001  label="top-side-gap"
  Placement = pos=(0,0,28.5) rot=(0,0,1;0rad)
  shape: bbox 44.1 x 24.8 x 0.4 mm, 14 faces (baked)
FEATURE [Part::MultiFuse] Fusion004  label="side-gaps"
  Shapes = -> [Pad002001003004001007,Pad002001003004001007001]
FEATURE [PartDesign::Fillet] Fillet003005005  label="servo-body-final-3"
  Base = -> Pad002001003003 [Edge31,Edge38,Edge25,Edge32]
  Radius = 2
FEATURE [Part::Cut] Cut001002002  label="servo-body-final-4"
  Base = -> Fillet003005005
  Tool = -> Fusion004
FEATURE [Part::Fillet] Fillet003005006  label="servo-body-final-5"
  Base = -> Cut001002002
  Edges = 3 edges r=0.3: [Edge1,Edge3,Edge14]
FEATURE [App::DocumentObjectGroup] Group  label="Servo-body-src"
  Group = -> [Pad,Pocket,Mirrored,Pocket001,Pocket002,Pocket003,Pocket004,Pocket005,Pocket006,Pad001,Pad002,Cut,Pad002001003003,Pad002001003004,Pad002001003004001007,Pad002001003004001007001,Fusion004,Fillet003005005,Cut001002002,Fillet003005006]
FEATURE [Part::Feature] Fillet003005006001  label="servo-body"
  shape: bbox 41.26 x 21.13 x 39.7 mm, 208 faces (baked)
FEATURE [Part::MultiFuse] Fusion005  label="servo-1"
  Shapes = -> [Fillet002,Fillet003005001,Fillet003001,Fillet003005006001]
FEATURE [Part::Feature] Cut001002003  label="bottom-screw-1"
  Placement = pos=(-18.1075,7.95754,34.2) rot=(1,0,0;3.14159rad)
  shape: bbox 3.75 x 3.75 x 33.19 mm, 18 faces (baked)
FEATURE [Part::Feature] Cut001002004  label="bottom-screw-2"
  Placement = pos=(18.1075,-7.95754,34.2) rot=(1,0,0;3.14159rad)
  shape: bbox 3.75 x 3.75 x 33.19 mm, 18 faces (baked)
FEATURE [Part::Feature] Cut001002005  label="bottom-screw-3"
  Placement = pos=(18.1075,7.95754,34.2) rot=(1,0,0;3.14159rad)
  shape: bbox 3.75 x 3.75 x 33.19 mm, 18 faces (baked)
FEATURE [Part::Feature] Cut001002006  label="bottom-screw-4"
  Placement = pos=(-18.1075,-7.95754,34.2) rot=(1,0,0;3.14159rad)
  shape: bbox 3.75 x 3.75 x 33.19 mm, 18 faces (baked)
FEATURE [Part::Compound] Compound  label="bottom-screws"
  Links = -> [Cut001002003,Cut001002006,Cut001002004,Cut001002005]
FEATURE [Part::Cylinder] Cylinder  label="wire-center"
  Angle = 360
  Height = 10
  Placement = pos=(1.5,0,0) rot=(0,1,0;1.5708rad)
  Radius = 0.65
FEATURE [Part::Feature] Cylinder001  label="wire-right"
  Placement = pos=(1.5,1.2,0) rot=(0,1,0;1.5708rad)
  shape: bbox 10 x 1.3 x 1.3 mm, 3 faces (baked)
FEATURE [Part::Feature] Cylinder002  label="wire-left"
  Placement = pos=(1.5,-1.2,0) rot=(0,1,0;1.5708rad)
  shape: bbox 10 x 1.3 x 1.3 mm, 3 faces (baked)
FEATURE [Part::MultiFuse] Fusion006  label="wires"
  Placement = pos=(20.55,0,6.35) rot=(0,0,1;0rad)
  Shapes = -> [Cylinder,Cylinder001,Cylinder002]
FEATURE [Part::Compound] Compound001  label="Servo-SM-S4303R-assembly"
  Links = -> [Chamfer001001,Fusion005,Fusion006,Compound]
FEATURE [Part::Feature] Chamfer001002  label="shaft001"
  Placement = pos=(10.55,0,41.9) rot=(0,0,1;0rad)
  shape: bbox 6 x 6 x 4.4 mm, 90 faces (baked)
FEATURE [Part::Feature] Fusion007  label="wires001"
  Placement = pos=(20.55,0,6.35) rot=(0,0,1;0rad)
  shape: bbox 10 x 3.7 x 1.3 mm, 9 faces (baked)
FEATURE [Part::Feature] Fusion008  label="servo-002"
  shape: bbox 56.13 x 21.13 x 45.15 mm, 371 faces (baked)
FEATURE [Part::Feature] Compound003  label="bottom-screws001"
  shape: bbox 39.97 x 19.67 x 33.19 mm, 72 faces, 4 solids (baked)
FEATURE [Part::Compound] Compound002  label="Servo-SM-S4303R-compound"
  Links = -> [Compound003,Fusion008,Fusion007,Chamfer001002]
FEATURE [Part::Compound] Compound004  label="Servo-SM-S4303R"
